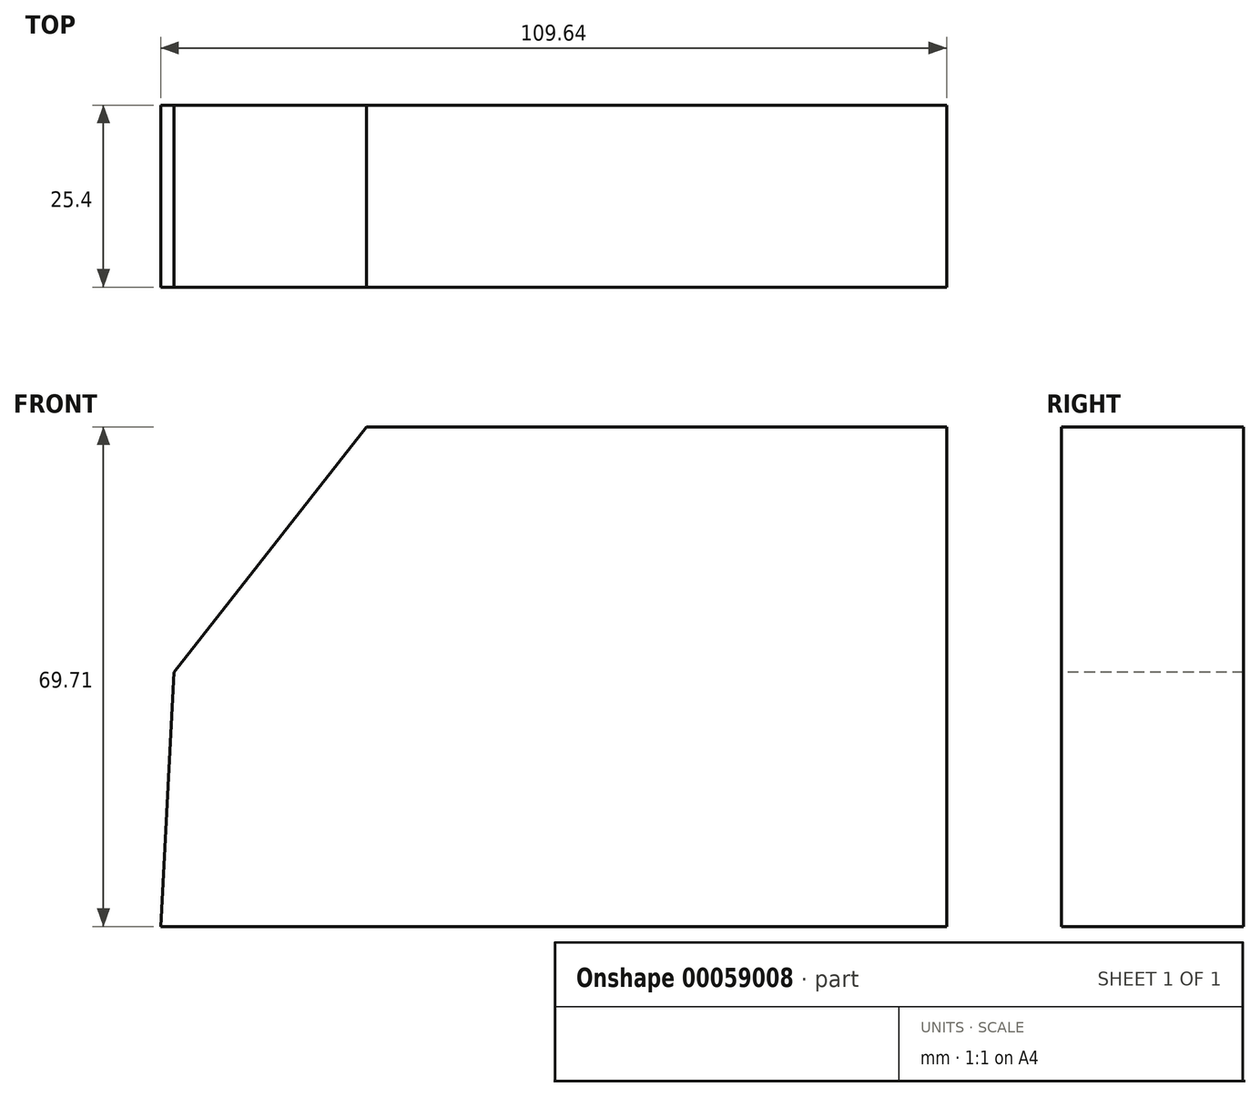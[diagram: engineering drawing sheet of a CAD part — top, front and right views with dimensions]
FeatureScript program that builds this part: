
annotation { "Feature Type Name" : "Feature", "Feature Type Description" : "" }
export const myFeature = defineFeature(function(context is Context, id is Id, definition is map)
    precondition{}
    {
        {
            var Q0;
            Q0=qCreatedBy(makeId("Front.planeOp"),FACE);
            var sketch = newSketch(context, id + "F0", { "sketchPlane" : qUnion([Q0])});
            skLineSegment(sketch, "E0", {"start": v(-120.67, 32.5) * mm, "end": v(-39.73, 32.5) * mm});
            skLineSegment(sketch, "E1", {"start": v(-39.73, 32.5) * mm, "end": v(-39.73, -37.22) * mm});
            skLineSegment(sketch, "E2", {"start": v(-39.73, -37.22) * mm, "end": v(-149.37, -37.22) * mm});
            skLineSegment(sketch, "E3", {"start": v(-149.37, -37.22) * mm, "end": v(-147.53, -1.75) * mm});
            skLineSegment(sketch, "E4", {"start": v(-147.53, -1.75) * mm, "end": v(-120.67, 32.5) * mm});
            skSolve(sketch);
        }
        {
            var Q0;
            Q0=makeQuery(id+"F0.imprint","IMPRINT",FACE,{"disambiguationData":[TD([[makeQuery(id+"F0.imprint","IMPRINT",EDGE,{"derivedFrom":sQuery(id+"F0.wireOp",EDGE,"E0")}),-1.0]])]});
            extrude(context, id + "F1", {"entities" : qUnion([Q0]), "oppositeDirection" : true, "depth" : 25.4 * mm});
        }
    });
